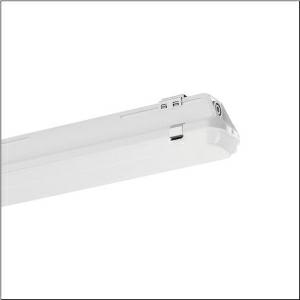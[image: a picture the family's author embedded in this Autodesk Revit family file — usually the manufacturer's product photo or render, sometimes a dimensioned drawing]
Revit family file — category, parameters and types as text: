
# Revit family: monsun_r__12_emergency_51fp207p437h3g_840e
name_source: partatom
category: Lighting Fixtures
units: mm (PartAtom-declared; Revit-internal decimal feet)

## family parameters
Cut with Voids When Loaded = No
Host = Face
Light Source = No
Part Type = Normal
Room Calculation Point = No
Round Connector Dimension = Use Diameter
Shared = No

## types (1)
- Monsun® 12 emergency (1 x LED, 3990 lm, 27.5 W, 4000K)
    Apparent Load = 28 VA
    CIE Flux Codes = 45 75 93 94 100
    Color Rendering = 80
    Color Temperature = 4000K
    Default Elevation = 1800 mm
    Description = Monsun® 12 emergency, damp-proof luminaire, chain hanger, primary optical cover: enclosure, of PC, light emission: direct distribution, primary light characteristic: symmetric, installation type: suspended mounting, surface-mounted, horizontal mounting, vertical mounting, LED rated luminous flux: 3.990 lm, light colour: 840, colour temperature: 4000K, control gear: ECG, with terminal, 4-pole, max. 2.5mm², mains connection: 220..240V, AC, 50/60Hz, rated input power: 28W, control gear: single battery element, battery: NiCd, 4,5 Ah, mains connection: 230V, luminaire housing, of glass-fibre reinforced polyester, uncoated, bright grey, length: 1.590 mm, width: 90 mm, height: 88mm, clip for enclosure, of stainless steel (V2A), ceiling mounting element, of stainless steel (V2A), chain hanger, of stainless steel (V2A), protection rating (complete): IP66, insulation class (complete): insulation class I (protective earthing), certification: CE, protection symbol: D, impact resistance: IK08, permissible ambient temperature for indoor applications: +5..+35°C, standard: EN 50419, EN 60598-2-1, EN 60598-2-22, no direct snow, no direct sun, no direct rain, for indoor or canopied outdoor use, corresponds to IFS (International Featured Standards) requirements for safety and quality in the food industry, packaging unit: 1 piece
    Height = 89 mm
    Lamp = 1 x LED
    Lamp Light Flux = 3990 lm
    Lamp Power = 27.5 W
    Lamp count = 1
    Length = 1590 mm
    Luminous efficacy = 145 lm/W
    Manufacturer = Siteco
    ModVariant = No
    Model = 51FP207P437H3G
    Mounting Place = Ceiling
    Mounting Type = Pendant
    Number of Poles = 1
    OnlyDefault = Yes
    Power Factor = 1
    Product Name = Monsun® 12 emergency
    Product group = damp-proof luminaire | ceiling pendant
    ProductGroupID = 908
    Protection Class = Protection class I
    Protection Degree = IP 66
    RLX_Detail_Level = 1
    RlxData = <blob elided: 88689 chars, md5=f8a64528>
    Socket = socket
    Standby Power = 0 W
    System Light Flux = 3990 lm
    System Power = 28 W
    Type Comments = Product without accessories
    Type Image = l_1004748.jpg
    URL = http://relux.com
    VarID = ---
    Voltage = 0 V
    Weight = 0.00 kg
    Width = 90 mm

## geometry (parser evidence)
native form markers: Blend x4, Sweep x13
no freeform markers — native parametric forms only
